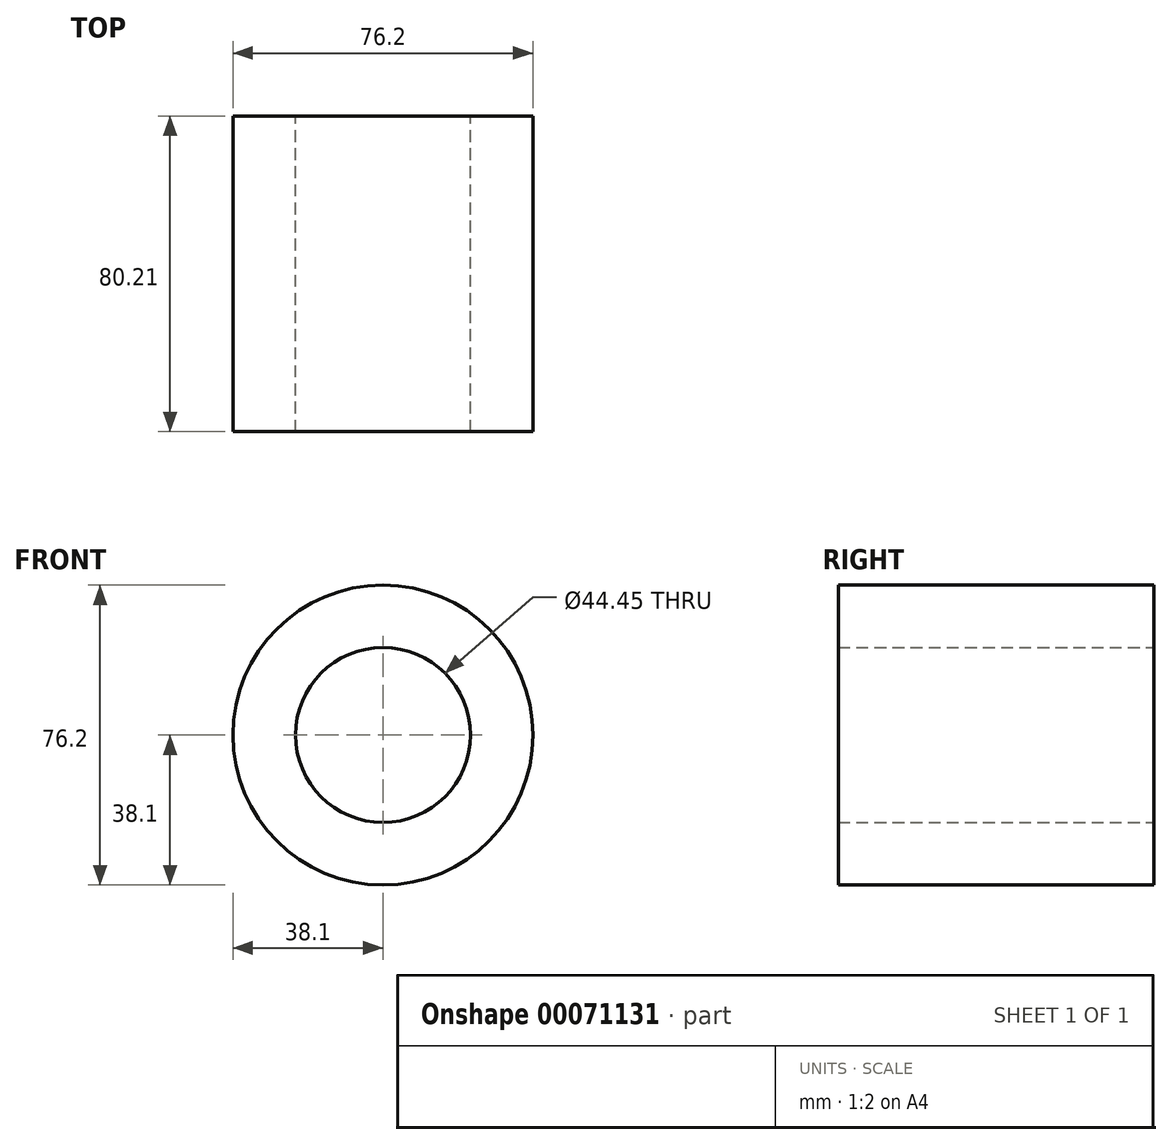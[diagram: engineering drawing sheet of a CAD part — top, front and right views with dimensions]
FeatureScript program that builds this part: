
annotation { "Feature Type Name" : "Feature", "Feature Type Description" : "" }
export const myFeature = defineFeature(function(context is Context, id is Id, definition is map)
    precondition{}
    {
        {
            var Q0;
            Q0=qCreatedBy(makeId("Front.planeOp"),FACE);
            var sketch = newSketch(context, id + "F0", { "sketchPlane" : qUnion([Q0])});
            skCircle(sketch, "E0", {"center": v(0, 0) * mm, "radius": 38.1 * mm});
            skCircle(sketch, "E1", {"center": v(0, 0) * mm, "radius": 22.23 * mm});
            skSolve(sketch);
        }
        {
            var Q0;
            Q0 = qSketchRegion(id + "F0", true);
            extrude(context, id + "F1", {"entities" : qUnion([Q0]), "depth" : 80.2 * mm});
        }
    });
